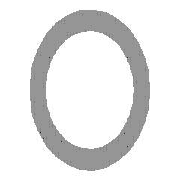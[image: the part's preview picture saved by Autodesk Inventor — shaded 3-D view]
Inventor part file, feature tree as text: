
AUTODESK INVENTOR PART (.ipt)
format: ipt  version: 2013 (Build 170138000, 138)  size: 119,808 bytes
history: native  units: mm (DEFAULTED — no unit token found)
features: other x4, plane x4, sketch x4, extrude x1
ambient origin geometry x8: Origin, YZ Plane, XZ Plane, XY Plane, X Axis, Y Axis, Z Axis, Center Point
bodies: Solid1 (feature_tree), Body (feature_tree)
feature tree (13):
  parser-record x1  (decoder bookkeeping rows leaked as tree rows — omitted from the tree; the rows remain in map.json)
  other  "Driven Length"
  other  "Start plane"
  other  "End plane"
  plane  "Work Plane4"
  plane  "Work Plane5"
  plane  "Work Plane6"
  extrude  "Extrusion2"  Depth=3.3782mm
  sketch  "Sketch"  dims[d5=1473.2mm d6=90.0deg d7=1473.2mm d8=3.302mm d9=0.0mm]
  sketch  "Sketch3"  dims[d0=33.401mm d1=3.3782mm]
  plane  "Work Plane3"
  sketch  "Sketch4"  dims[d2=1473.2mm d3=0.0mm]
  sketch  "Sketch5"  dims[d4=-0.0mm]
